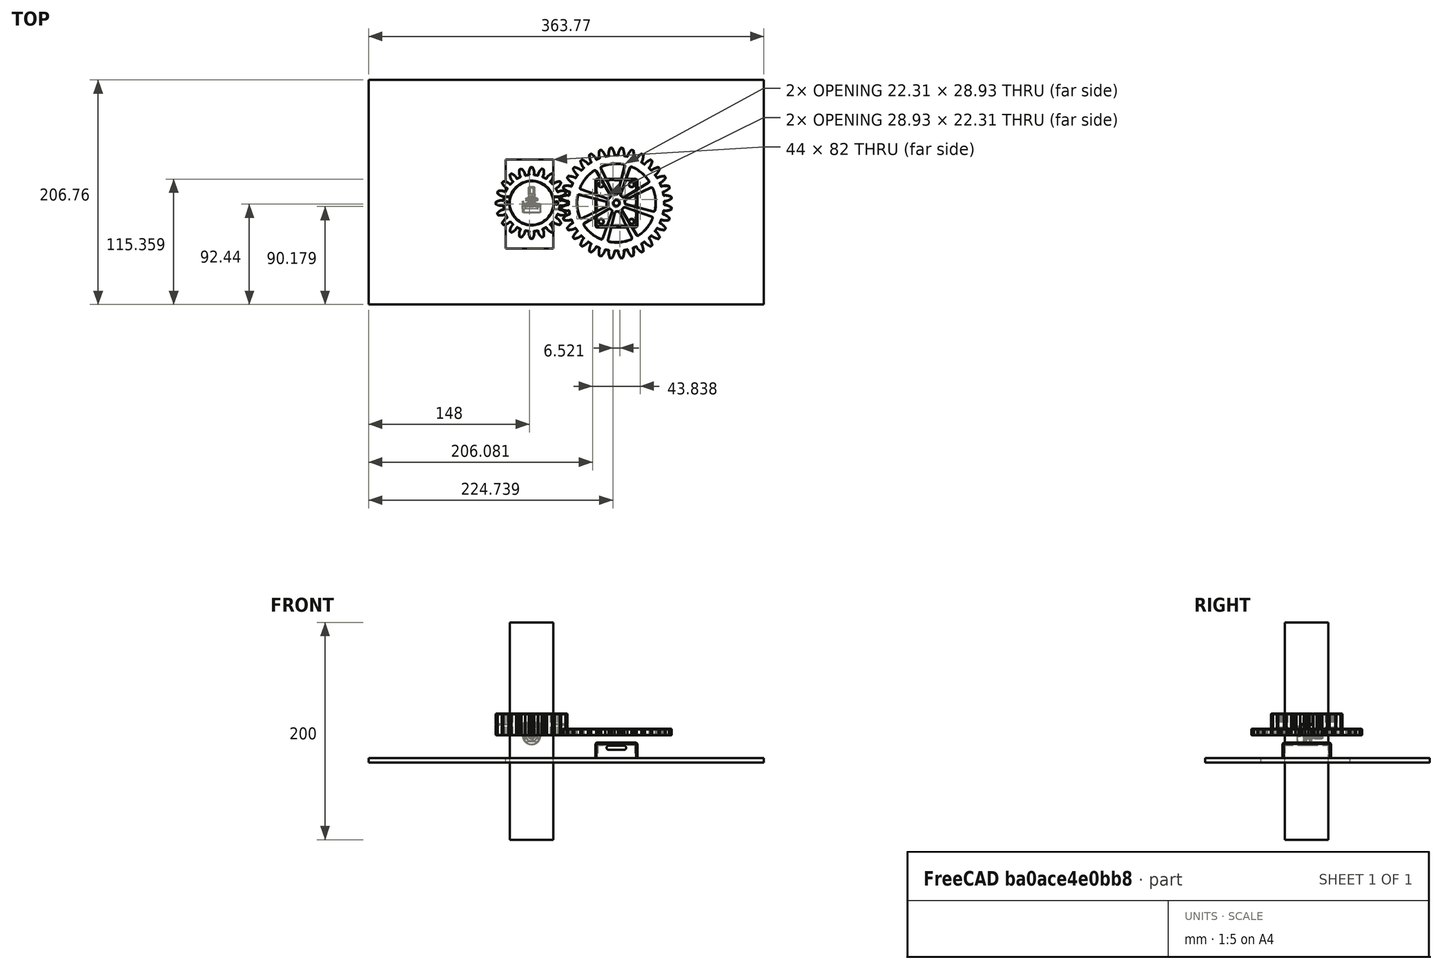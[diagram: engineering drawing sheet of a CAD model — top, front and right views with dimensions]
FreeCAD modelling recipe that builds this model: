
FCSTD DOCUMENT  (FreeCAD 0.19R24212 (Git))
Label: Boitier capteur angle barre
License: Creative Commons Attribution
LicenseURL: http://creativecommons.org/licenses/by/4.0/
objects: Sketcher::SketchObject×12, PartDesign::Pocket×11, Part::Feature×9, PartDesign::Chamfer×7, PartDesign::Body×5, PartDesign::SubShapeBinder×4, Mesh::Feature×4, PartDesign::FeaturePython×2, App::Part×2, PartDesign::Mirrored×2, Part::Cylinder×1, PartDesign::PolarPattern×1, PartDesign::FeatureBase×1, PartDesign::Pad×1, PartDesign::AdditiveBox×1, PartDesign::Thickness×1, PartDesign::MultiTransform×1, App::DocumentObjectGroup×1
note: 80 computed .brp shape members not serialized (recipe doc carries the construction recipe); baked Part::Feature solids carry a one-line shape summary decoded from their .brp

FEATURE [PartDesign::FeaturePython] involutegear  # WARN: FeaturePython — macro-defined, semantics opaque (R4)
  backlash = 0
  beta = 0
  clearance = 0.25
  double_helix = false
  dw = 60
  head = 0
  height = 20
  module = 3
  numpoints = 6
  pressure_angle = 20
  properties_from_tool = false
  reversed_backlash = false
  shift = 0
  simple = false
  teeth = 20
  transverse_pitch = 9.42478
  undercut = false
FEATURE [Part::Cylinder] Cylinder  label="Cylindre"
  Angle = 360
  AttacherType = Attacher::AttachEngine3D
  Height = 200
  Placement = pos=(0,0,-96) rot=(0,0,1;0rad)
  Radius = 20
FEATURE [Sketcher::SketchObject] Sketch
  FullyConstrained = true
  MapMode = 5
  Support = -> [XY_Plane]
  sketch-geometry (1):
    g0: Circle CenterX=0 CenterY=0 CenterZ=0 NormalX=0 NormalY=0 NormalZ=1 AngleXU=0 Radius=20.2
  constraints (2):
    c: Coincident(g0,g-1)
    c: Diameter(g0) = 40.4
FEATURE [PartDesign::Pocket] Pocket
  BaseFeature = -> involutegear
  Length = 5
  Length2 = 100
  Profile = -> Sketch
  Refine = true
  Reversed = true
  Type = 1
FEATURE [PartDesign::FeaturePython] involutegear001  # WARN: FeaturePython — macro-defined, semantics opaque (R4)
  backlash = 0
  beta = 0
  clearance = 0.25
  double_helix = false
  dw = 96
  head = 0
  height = 6
  module = 3
  numpoints = 6
  pressure_angle = 20
  properties_from_tool = false
  reversed_backlash = false
  shift = 0
  simple = false
  teeth = 32
  transverse_pitch = 9.42478
  undercut = false
  expr: module = involutegear.module
FEATURE [Part::Feature] Part__Feature  label="Potentiometer B"
  shape: bbox 17.05 x 8.301 x 11 mm, 69 faces (baked)
FEATURE [Part::Feature] Part__Feature001  label="Potentiometer B001"
  shape: bbox 17 x 1.2 x 20 mm, 40 faces (baked)
FEATURE [Part::Feature] Part__Feature002  label="Potentiometer B002"
  shape: bbox 3.5 x 1.7 x 9.5 mm, 38 faces (baked)
FEATURE [Part::Feature] Part__Feature003  label="Potentiometer B003"
  shape: bbox 3.5 x 1.7 x 9.5 mm, 38 faces (baked)
FEATURE [Part::Feature] Part__Feature004  label="Potentiometer B004"
  shape: bbox 3.5 x 1.7 x 9.5 mm, 38 faces (baked)
FEATURE [Part::Feature] Part__Feature005  label="Potentiometer B005"
  shape: bbox 18.32 x 8.103 x 18.4 mm, 83 faces (baked)
FEATURE [App::Part] Potentiom___e_B  label="Potentiometer B006"
  Group = -> [Part__Feature,Part__Feature001,Part__Feature002,Part__Feature003,Part__Feature004,Part__Feature005]
  Origin = -> Origin002
FEATURE [Part::Feature] Part__Feature006  label="Potentiometer A"
  Placement = pos=(0,6.5,0) rot=(0,-1,0;1.27695rad)
  shape: bbox 6.211 x 12.4 x 6.211 mm, 738 faces (baked)
FEATURE [Part::Feature] Part__Feature007  label="Potentiometer Ecrou"
  Placement = pos=(0,2.7,0) rot=(0,-1,0;1.13434rad)
  shape: bbox 11.53 x 2.813 x 11.53 mm, 38 faces (baked)
FEATURE [Part::Feature] Part__Feature008  label="Potentiometer Rondelle"
  Placement = pos=(0,2.4,0) rot=(0,1,0;0.012725rad)
  shape: bbox 11.45 x 0.3 x 11.45 mm, 6 faces (baked)
FEATURE [App::Part] Potentiom___e_10K  label="Potentiometer 10K"
  Group = -> [Potentiom___e_B,Part__Feature006,Part__Feature007,Part__Feature008]
  Origin = -> Origin003
  Placement = pos=(78,0,-9) rot=(1,0,0;1.5708rad)
  expr: .Placement.Base.x = involutegear.dw / 2 + involutegear001.dw / 2
FEATURE [Sketcher::SketchObject] Sketch001
  FullyConstrained = true
  MapMode = 5
  Support = -> [XY_Plane001]
  sketch-geometry (1):
    g0: Circle CenterX=0 CenterY=0 CenterZ=0 NormalX=0 NormalY=0 NormalZ=1 AngleXU=0 Radius=2.5
  constraints (2):
    c: Coincident(g0,g-1)
    c: Diameter(g0) = 5
FEATURE [PartDesign::Pocket] Pocket001
  BaseFeature = -> involutegear001
  Length = 5
  Length2 = 100
  Profile = -> Sketch001
  Refine = true
  Reversed = true
  Type = 1
FEATURE [Sketcher::SketchObject] Sketch002
  FullyConstrained = true
  MapMode = 5
  Support = -> [XY_Plane001]
  sketch-geometry (9):
    g0: LineSegment StartX=0 StartY=0 StartZ=0 EndX=11.9707 EndY=32.8892 EndZ=0
    g1: LineSegment StartX=1.92307 StartY=8.79215 StartZ=0 EndX=10.728 EndY=32.9835 EndZ=0
    g2: LineSegment StartX=-1.92307 StartY=8.79215 StartZ=0 EndX=-10.728 EndY=32.9835 EndZ=0
    g3: ArcOfCircle CenterX=0 CenterY=0 CenterZ=0 NormalX=0 NormalY=0 NormalZ=1 AngleXU=0 Radius=36 StartAngle=1.29229 EndAngle=1.8493
    g4: ArcOfCircle CenterX=0 CenterY=0 CenterZ=0 NormalX=0 NormalY=0 NormalZ=1 AngleXU=0 Radius=8 StartAngle=1.48979 EndAngle=1.6518
    g5: ArcOfCircle CenterX=-9.55338 CenterY=33.411 CenterZ=0 NormalX=0 NormalY=0 NormalZ=1 AngleXU=0 Radius=1.25 StartAngle=1.8493 EndAngle=3.49066
    g6: ArcOfCircle CenterX=9.55338 CenterY=33.411 CenterZ=0 NormalX=0 NormalY=0 NormalZ=1 AngleXU=0 Radius=1.25 StartAngle=5.93412 EndAngle=7.57548
    g7: ArcOfCircle CenterX=0.74845 CenterY=9.21967 CenterZ=0 NormalX=0 NormalY=0 NormalZ=1 AngleXU=0 Radius=1.25 StartAngle=4.63139 EndAngle=5.93412
    g8: ArcOfCircle CenterX=-0.74845 CenterY=9.21967 CenterZ=0 NormalX=0 NormalY=0 NormalZ=1 AngleXU=0 Radius=1.25 StartAngle=3.49066 EndAngle=4.79339
  constraints (23):
    c: Coincident(g3,g4)
    c: Coincident(g3,g-1)
    c: Parallel(g1,g0)
    c: Radius(g3) = 36
    c: Radius(g4) = 8
    c: Angle(g0) = 1.22173
    c: Coincident(g0,g3)
    c: Distance(g0) = 35
    c: Tangent(g2,g5) = 1.5708
    c: Tangent(g3,g5) = -1.5708
    c: Tangent(g3,g6) = -1.5708
    c: Tangent(g1,g6) = -1.5708
    c: Distance(g0,g1) = 1.2
    c: Tangent(g4,g7) = 1.5708
    c: Tangent(g1,g7) = -1.5708
    c: Tangent(g2,g8) = 1.5708
    c: Tangent(g4,g8) = 1.5708
    c: Equal(g5,g6)
    c: Equal(g6,g8)
    c: Equal(g8,g7)
    c: Radius(g6) = 1.25
    c: Horizontal(g5,g6)
    c: Horizontal(g8,g7)
FEATURE [PartDesign::Pocket] Pocket002
  BaseFeature = -> Pocket001
  Length = 5
  Length2 = 100
  Profile = -> Sketch002
  Refine = true
  Reversed = true
  Type = 1
FEATURE [PartDesign::PolarPattern] PolarPattern
  Angle = 360
  Axis = -> Z_Axis001
  BaseFeature = -> Pocket002
  Occurrences = 8
  Originals = -> [Pocket002]
  Refine = true
FEATURE [Sketcher::SketchObject] Sketch003
  ExternalGeometry = -> [Pocket]
  FullyConstrained = true
  MapMode = 5
  Placement = pos=(0,0,0) rot=(0.57735,0.57735,0.57735;2.0944rad)
  Support = -> [YZ_Plane]
  expr: Constraints[12] = involutegear.height / 2
  sketch-geometry (6):
    g0: LineSegment StartX=5.74684 StartY=21.4937 StartZ=0 EndX=5.74684 EndY=10 EndZ=0
    g1: LineSegment StartX=5.74684 StartY=10 StartZ=0 EndX=-5.74684 EndY=10 EndZ=0
    g2: LineSegment StartX=-5.74684 StartY=10 StartZ=0 EndX=-5.74684 EndY=-1.49369 EndZ=0
    g3: LineSegment StartX=-5.74684 StartY=-1.49369 StartZ=0 EndX=-44.2532 EndY=-1.49369 EndZ=0
    g4: LineSegment StartX=-44.2532 StartY=-1.49369 StartZ=0 EndX=-44.2532 EndY=21.4937 EndZ=0
    g5: LineSegment StartX=-44.2532 StartY=21.4937 StartZ=0 EndX=5.74684 EndY=21.4937 EndZ=0
  constraints (18):
    c: Vertical(g0)
    c: Coincident(g0,g1)
    c: Horizontal(g1)
    c: Coincident(g1,g2)
    c: Vertical(g2)
    c: Coincident(g2,g3)
    c: Horizontal(g3)
    c: Coincident(g3,g4)
    c: Vertical(g4)
    c: Coincident(g4,g5)
    c: Coincident(g5,g0)
    c: Horizontal(g5)
    c: DistanceY(g0) = 10
    c: Equal(g1,g0)
    c: Equal(g0,g2)
    c: DistanceX(g5,g5) = 50
    c: PointOnObject(g1,g-3)
    c: PointOnObject(g0,g-4)
FEATURE [PartDesign::Pocket] Pocket003
  BaseFeature = -> Pocket
  Length = 5
  Length2 = 100
  Midplane = true
  Profile = -> Sketch003
  Refine = true
  Type = 1
FEATURE [PartDesign::FeatureBase] Clone
  BaseFeature = -> Pocket
FEATURE [PartDesign::SubShapeBinder] Binder
  BindMode = 0
  ClaimChildren = false
  Context = -> Body002 [Binder.]
  Fuse = false
  MakeFace = true
  PartialLoad = false
  Relative = true
  Support = -> [Body[Sketch003.Edge2]]
  _Version = 2
FEATURE [Sketcher::SketchObject] Sketch004
  ExternalGeometry = -> [Binder]
  FullyConstrained = true
  MapMode = 5
  Placement = pos=(0,0,0) rot=(0.57735,0.57735,0.57735;2.0944rad)
  Support = -> [YZ_Plane004]
  sketch-geometry (6):
    g0: LineSegment StartX=5.74684 StartY=21.4937 StartZ=0 EndX=5.74684 EndY=10 EndZ=0
    g1: LineSegment StartX=5.74684 StartY=10 StartZ=0 EndX=-5.74684 EndY=10 EndZ=0
    g2: LineSegment StartX=-5.74684 StartY=10 StartZ=0 EndX=-5.74684 EndY=-1.49369 EndZ=0
    g3: LineSegment StartX=-5.74684 StartY=-1.49369 StartZ=0 EndX=44.2532 EndY=-1.49369 EndZ=0
    g4: LineSegment StartX=44.2532 StartY=-1.49369 StartZ=0 EndX=44.2532 EndY=21.4937 EndZ=0
    g5: LineSegment StartX=44.2532 StartY=21.4937 StartZ=0 EndX=5.74684 EndY=21.4937 EndZ=0
  constraints (16):
    c: Vertical(g0)
    c: Coincident(g0,g1)
    c: Coincident(g1,g2)
    c: Vertical(g2)
    c: Coincident(g2,g3)
    c: Horizontal(g3)
    c: Coincident(g3,g4)
    c: Vertical(g4)
    c: Coincident(g4,g5)
    c: Coincident(g5,g0)
    c: Horizontal(g5)
    c: Equal(g2,g1)
    c: Equal(g1,g0)
    c: Coincident(g-3,g1)
    c: Coincident(g-3,g0)
    c: DistanceX(g3,g3) = 50
FEATURE [PartDesign::Pocket] Pocket004
  BaseFeature = -> Clone
  Length = 5
  Length2 = 100
  Midplane = true
  Profile = -> Sketch004
  Refine = true
  Type = 1
FEATURE [Sketcher::SketchObject] Sketch005
  AttachmentOffset = pos=(0,0,10) rot=(0,0,1;0rad)
  FullyConstrained = true
  MapMode = 5
  Placement = pos=(0,0,10) rot=(0,0,1;0rad)
  Support = -> [XY_Plane]
  expr: .AttachmentOffset.Base.z = involutegear.height / 2
  sketch-geometry (3):
    g0: Circle CenterX=-23 CenterY=0 CenterZ=0 NormalX=0 NormalY=0 NormalZ=1 AngleXU=0 Radius=1.6
    g1: Circle CenterX=23 CenterY=0 CenterZ=0 NormalX=0 NormalY=0 NormalZ=1 AngleXU=0 Radius=1.6
    g2: Circle CenterX=-23 CenterY=0 CenterZ=0 NormalX=0 NormalY=0 NormalZ=1 AngleXU=0 Radius=2.9
  constraints (7):
    c: PointOnObject(g0,g-1)
    c: Equal(g0,g1)
    c: Diameter(g0) = 3.2
    c: Coincident(g2,g0)
    c: Diameter(g2) = 5.8
    c: DistanceX(g0) = -23
    c: Symmetric(g0,g1,g-2)
FEATURE [PartDesign::Pocket] Pocket005
  BaseFeature = -> Pocket003
  Length = 5
  Length2 = 100
  Profile = -> Sketch005
  Refine = true
  Type = 1
FEATURE [PartDesign::SubShapeBinder] Binder001
  BindMode = 0
  ClaimChildren = false
  Context = -> Body002 [Binder001.]
  Fuse = false
  MakeFace = true
  PartialLoad = false
  Relative = true
  Support = -> [Body[Pocket005.Edge297]]
  _Version = 2
FEATURE [Sketcher::SketchObject] Sketch006
  AttachmentOffset = pos=(0,0,20) rot=(0,0,1;0rad)
  ExternalGeometry = -> [Binder001]
  FullyConstrained = true
  MapMode = 5
  Placement = pos=(0,0,20) rot=(0,0,1;0rad)
  Support = -> [XY_Plane004]
  expr: .AttachmentOffset.Base.z = involutegear.height
  sketch-geometry (2):
    g0: Circle CenterX=-23 CenterY=0 CenterZ=0 NormalX=0 NormalY=0 NormalZ=1 AngleXU=0 Radius=1.1
    g1: Circle CenterX=23 CenterY=0 CenterZ=0 NormalX=0 NormalY=0 NormalZ=1 AngleXU=0 Radius=1.1
  constraints (4):
    c: Coincident(g0,g-3)
    c: Symmetric(g1,g0,g-2)
    c: Equal(g0,g1)
    c: Diameter(g0) = 2.2
FEATURE [PartDesign::Pocket] Pocket006
  BaseFeature = -> Pocket004
  Length = 5
  Length2 = 100
  Profile = -> Sketch006
  Refine = true
  Type = 1
FEATURE [Sketcher::SketchObject] Sketch007
  FullyConstrained = false
  MapMode = 5
  Support = -> [XY_Plane005]
  sketch-geometry (8):
    g0: LineSegment StartX=-149.999 StartY=-93.4428 StartZ=0 EndX=213.771 EndY=-93.4428 EndZ=0
    g1: LineSegment StartX=213.771 StartY=-93.4428 StartZ=0 EndX=213.771 EndY=113.318 EndZ=0
    g2: LineSegment StartX=213.771 StartY=113.318 StartZ=0 EndX=-149.999 EndY=113.318 EndZ=0
    g3: LineSegment StartX=-149.999 StartY=113.318 StartZ=0 EndX=-149.999 EndY=-93.4428 EndZ=0
    g4: LineSegment StartX=-24 StartY=40 StartZ=0 EndX=20 EndY=40 EndZ=0
    g5: LineSegment StartX=20 StartY=40 StartZ=0 EndX=20 EndY=-42 EndZ=0
    g6: LineSegment StartX=20 StartY=-42 StartZ=0 EndX=-24 EndY=-42 EndZ=0
    g7: LineSegment StartX=-24 StartY=-42 StartZ=0 EndX=-24 EndY=40 EndZ=0
  constraints (20):
    c: Coincident(g0,g1)
    c: Coincident(g1,g2)
    c: Coincident(g2,g3)
    c: Coincident(g3,g0)
    c: Horizontal(g0)
    c: Horizontal(g2)
    c: Vertical(g1)
    c: Vertical(g3)
    c: Coincident(g4,g5)
    c: Coincident(g5,g6)
    c: Coincident(g6,g7)
    c: Coincident(g7,g4)
    c: Horizontal(g4)
    c: Horizontal(g6)
    c: Vertical(g5)
    c: Vertical(g7)
    c: DistanceX(g4) = 20
    c: DistanceY(g5) = -42
    c: DistanceX(g4) = -24
    c: DistanceY(g4) = 40
FEATURE [PartDesign::Pad] Pad
  Direction = (1,1,1)
  Length = 4
  Length2 = 100
  Profile = -> Sketch007
  Refine = true
  Type = 0
FEATURE [PartDesign::Body] Body003  label="Tole support"
  Group = -> [Sketch007,Pad]
  Origin = -> Origin005
  Placement = pos=(0,0,-25) rot=(0,0,1;0rad)
  Tip = -> Pad
FEATURE [PartDesign::AdditiveBox] Box
  AttacherType = Attacher::AttachEngine3D
  AttachmentOffset = pos=(-17,-20,0) rot=(0,0,1;0rad)
  Height = 12
  Length = 34
  MapMode = 5
  Placement = pos=(17,-20,0) rot=(0,1,0;3.14159rad)
  Refine = true
  Support = -> [XY_Plane006]
  Width = 40
  expr: .AttachmentOffset.Base.y = -Width / 2
  expr: .AttachmentOffset.Base.x = -Length / 2
FEATURE [PartDesign::Thickness] Thickness
  Base = -> Box [Face6]
  BaseFeature = -> Box
  Intersection = false
  Join = 1
  Mode = 0
  Refine = true
  SupportTransform = false
  Value = 2.4
FEATURE [PartDesign::SubShapeBinder] Binder002
  BindMode = 0
  ClaimChildren = false
  Context = -> Body004 [Binder002.]
  Fuse = false
  MakeFace = true
  PartialLoad = false
  Relative = true
  Support = -> [Potentiom___e_10K[Potentiom___e_B.Part__Feature.Edge1,Potentiom___e_B.Part__Feature.Edge161,Potentiom___e_B.Part__Feature.Edge152,Potentiom___e_B.Part__Feature.Edge181,Potentiom___e_B.Part__Feature.Edge164,Potentiom___e_B.Part__Feature.Edge180,Potentiom___e_B.Part__Feature.Edge159,Potentiom___e_B.Part__Feature.Edge171]]
  _Version = 2
FEATURE [Sketcher::SketchObject] Sketch008
  ExternalGeometry = -> [Binder002]
  FullyConstrained = true
  MapMode = 5
  Support = -> [XY_Plane006]
  sketch-geometry (4):
    g0: LineSegment StartX=-8.85314 StartY=1.75606 StartZ=0 EndX=-8.85314 EndY=-1.75606 EndZ=0
    g1: LineSegment StartX=-8.85314 StartY=-1.75606 StartZ=0 EndX=-7.06011 EndY=-1.50036 EndZ=0
    g2: LineSegment StartX=-7.06011 StartY=-1.50036 StartZ=0 EndX=-7.06011 EndY=1.50036 EndZ=0
    g3: LineSegment StartX=-7.06011 StartY=1.50036 StartZ=0 EndX=-8.85314 EndY=1.75606 EndZ=0
  constraints (11):
    c: Vertical(g0)
    c: Coincident(g0,g1)
    c: Coincident(g1,g2)
    c: Coincident(g2,g3)
    c: Coincident(g0,g3)
    c: Parallel(g-3,g3)
    c: Parallel(g-5,g1)
    c: DistanceX(g-6,g2) = 0.4
    c: DistanceX(g0,g-4) = 0.4
    c: DistanceY(g-3,g2) = 0.4
    c: Symmetric(g1,g2,g-1)
FEATURE [PartDesign::Pocket] Pocket007
  BaseFeature = -> Thickness
  Length = 5
  Length2 = 100
  Profile = -> Sketch008
  Refine = true
  Reversed = true
  Type = 1
FEATURE [Sketcher::SketchObject] Sketch009
  FullyConstrained = true
  MapMode = 5
  Placement = pos=(0,0,0) rot=(1,0,0;1.5708rad)
  Support = -> [XZ_Plane006]
  sketch-geometry (4):
    g0: ArcOfCircle CenterX=-7 CenterY=-2.4 CenterZ=0 NormalX=0 NormalY=0 NormalZ=1 AngleXU=0 Radius=2 StartAngle=1.5708 EndAngle=4.71239
    g1: ArcOfCircle CenterX=7 CenterY=-2.4 CenterZ=0 NormalX=0 NormalY=0 NormalZ=1 AngleXU=0 Radius=2 StartAngle=4.71239 EndAngle=7.85398
    g2: LineSegment StartX=-7 StartY=-4.4 StartZ=0 EndX=7 EndY=-4.4 EndZ=0
    g3: LineSegment StartX=-7 StartY=-0.4 StartZ=0 EndX=7 EndY=-0.4 EndZ=0
  constraints (9):
    c: Tangent(g0,g3) = 1.5708
    c: Tangent(g0,g2) = -1.5708
    c: Tangent(g2,g1) = -1.5708
    c: Tangent(g3,g1) = 1.5708
    c: Horizontal(g2)
    c: Radius(g0) = 2
    c: Symmetric(g0,g1,g-2)
    c: Distance(g0,g1) = 14
    c: Distance(g-1,g3) = 0.4
FEATURE [PartDesign::Pocket] Pocket008
  BaseFeature = -> Pocket007
  Length = 5
  Length2 = 100
  Profile = -> Sketch009
  Refine = true
  Reversed = true
  Type = 1
FEATURE [Sketcher::SketchObject] Sketch010
  ExternalGeometry = -> [Box]
  FullyConstrained = true
  MapMode = 5
  Support = -> [XY_Plane006]
  sketch-geometry (1):
    g0: Circle CenterX=14 CenterY=17 CenterZ=0 NormalX=0 NormalY=0 NormalZ=1 AngleXU=0 Radius=2.1
  constraints (3):
    c: Radius(g0) = 2.1
    c: DistanceX(g0,g-3) = 3
    c: DistanceY(g0,g-3) = 3
FEATURE [PartDesign::Pocket] Pocket009
  BaseFeature = -> Pocket008
  Length = 5
  Length2 = 100
  Profile = -> Sketch010
  Refine = true
  Reversed = true
  Type = 0
FEATURE [PartDesign::Mirrored] Mirrored
  MirrorPlane = -> Sketch010 [H_Axis]
  Refine = true
FEATURE [PartDesign::Mirrored] Mirrored001
  MirrorPlane = -> Sketch010 [V_Axis]
  Refine = true
FEATURE [PartDesign::MultiTransform] MultiTransform
  BaseFeature = -> Pocket009
  Originals = -> [Pocket009]
  Refine = true
  Transformations = -> [Mirrored,Mirrored001]
FEATURE [PartDesign::SubShapeBinder] Binder003
  BindMode = 0
  ClaimChildren = false
  Context = -> Body004 [Binder003.]
  Fuse = false
  MakeFace = true
  PartialLoad = false
  Relative = true
  Support = -> [Potentiom___e_10K[Part__Feature008.Edge10]]
  _Version = 2
FEATURE [Sketcher::SketchObject] Sketch011
  ExternalGeometry = -> [Binder003]
  FullyConstrained = true
  MapMode = 5
  Support = -> [XY_Plane006]
  sketch-geometry (1):
    g0: Circle CenterX=0 CenterY=0 CenterZ=0 NormalX=0 NormalY=0 NormalZ=1 AngleXU=0 Radius=3.6
  constraints (2):
    c: Coincident(g0,g-1)
    c: Equal(g0,g-3)
FEATURE [PartDesign::Pocket] Pocket010
  BaseFeature = -> MultiTransform
  Length = 5
  Length2 = 100
  Profile = -> Sketch011
  Refine = true
  Reversed = true
  Type = 1
FEATURE [PartDesign::Chamfer] Chamfer
  Angle = 45
  Base = -> Pocket010 [Edge63,Edge61,Edge49,Edge58,Edge55,Edge53,Edge59,Edge51,Edge47]
  BaseFeature = -> Pocket010
  ChamferType = 0
  FlipDirection = false
  Refine = true
  Size = 0.4
  Size2 = 1
  SupportTransform = false
FEATURE [PartDesign::Chamfer] Chamfer001
  Angle = 45
  Base = -> Chamfer [Edge59,Edge19,Edge60,Edge64,Edge63,Edge20,Edge22,Edge21]
  BaseFeature = -> Chamfer
  ChamferType = 0
  FlipDirection = false
  Refine = true
  Size = 1.2
  Size2 = 1
  SupportTransform = false
FEATURE [PartDesign::Body] Body004  label="Boitier"
  Group = -> [Box,Thickness,Binder002,Sketch008,Pocket007,Sketch009,Pocket008,Sketch010,Pocket009,MultiTransform,Mirrored,Mirrored001,Sketch011,Binder003,Pocket010,Chamfer,Chamfer001]
  Origin = -> Origin006
  Placement = pos=(78,0,-9) rot=(0,0,1;0rad)
  Tip = -> Chamfer001
  expr: .Placement.Base.z = Potentiom___e_10K.Placement.Base.z
  expr: .Placement.Base.x = involutegear.dw / 2 + involutegear001.dw / 2
FEATURE [Mesh::Feature] Mesh005  label="Boitier (Meshed)001"
FEATURE [PartDesign::Chamfer] Chamfer002
  Angle = 45
  Base = -> Pocket005 [Face2,Face76]
  BaseFeature = -> Pocket005
  ChamferType = 0
  FlipDirection = false
  Refine = true
  Size = 0.4
  Size2 = 1
  SupportTransform = false
FEATURE [PartDesign::Chamfer] Chamfer003
  Angle = 45
  Base = -> Chamfer002 [Edge18,Edge19,Edge3,Edge7,Edge17,Edge15,Edge13,Edge11,Edge14,Edge16,Edge20,Edge266,Edge265,Edge263,Edge261,Edge109,Edge267,Edge259,Edge260,Edge262,Edge264,Edge108,Edge102,Edge268,Edge111,Edge110,Edge22]
  BaseFeature = -> Chamfer002
  ChamferType = 0
  FlipDirection = false
  Refine = true
  Size = 0.4
  Size2 = 1
  SupportTransform = false
FEATURE [PartDesign::Body] Body  label="Gear barre A"
  Group = -> [involutegear,Sketch,Pocket,Sketch003,Pocket003,Sketch005,Pocket005,Chamfer002,Chamfer003]
  Origin = -> Origin
  Tip = -> Chamfer003
FEATURE [Mesh::Feature] Mesh006  label="Gear barre A (Meshed)"
FEATURE [PartDesign::Chamfer] Chamfer004
  Angle = 45
  Base = -> Pocket006 [Face76,Face4]
  BaseFeature = -> Pocket006
  ChamferType = 0
  FlipDirection = false
  Refine = true
  Size = 0.4
  Size2 = 1
  SupportTransform = false
FEATURE [PartDesign::Chamfer] Chamfer005
  Angle = 45
  Base = -> Chamfer004 [Edge251,Edge99,Edge12,Edge14,Edge16,Edge20,Edge19,Edge3,Edge7,Edge17,Edge15,Edge13,Edge11,Edge110,Edge252,Edge255,Edge257,Edge259,Edge260,Edge258,Edge256,Edge254,Edge261,Edge109,Edge112]
  BaseFeature = -> Chamfer004
  ChamferType = 0
  FlipDirection = false
  Refine = true
  Size = 0.4
  Size2 = 1
  SupportTransform = false
FEATURE [PartDesign::Body] Body002  label="Gear barre B"
  BaseFeature = -> Pocket
  Group = -> [Clone,Sketch004,Pocket004,Binder,Binder001,Sketch006,Pocket006,Chamfer004,Chamfer005]
  Origin = -> Origin004
  Tip = -> Chamfer005
FEATURE [Mesh::Feature] Mesh  label="Gear barre B (Meshed)"
FEATURE [PartDesign::Chamfer] Chamfer006
  Angle = 45
  Base = -> PolarPattern [Face5,Face4]
  BaseFeature = -> PolarPattern
  ChamferType = 0
  FlipDirection = false
  Refine = true
  Size = 0.4
  Size2 = 1
  SupportTransform = false
FEATURE [PartDesign::Body] Body001  label="Gear capteur"
  Group = -> [involutegear001,Sketch001,Pocket001,Sketch002,Pocket002,PolarPattern,Chamfer006]
  Origin = -> Origin001
  Placement = pos=(78,0,0) rot=(0,0,1;0.097738rad)
  Tip = -> Chamfer006
  expr: .Placement.Base.x = involutegear.dw / 2 + involutegear001.dw / 2
FEATURE [Mesh::Feature] Mesh007  label="Gear capteur (Meshed)"
FEATURE [App::DocumentObjectGroup] Groupe  label="Maillages"
  Group = -> [Mesh005,Mesh006,Mesh,Mesh007]
